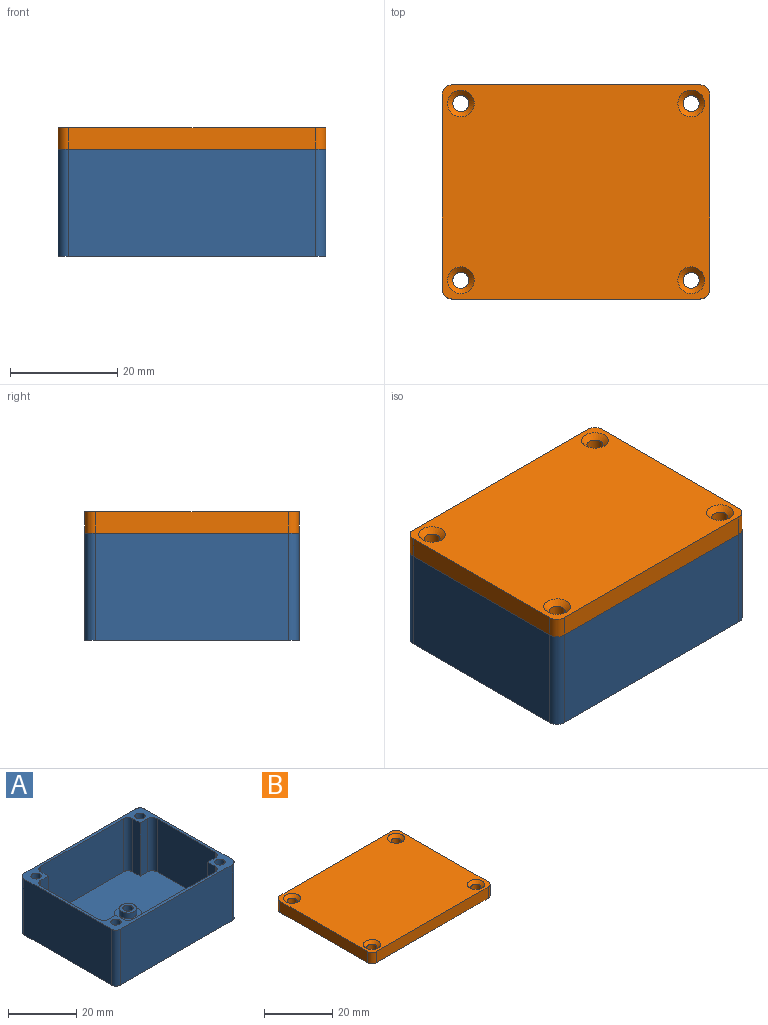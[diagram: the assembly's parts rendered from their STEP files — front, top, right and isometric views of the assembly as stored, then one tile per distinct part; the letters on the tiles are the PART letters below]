
ASSEMBLY  parts=2 mates=1
PART A: 47 faces, bbox 50x40x20 mm
  f0: plane 50x40mm, normal (0,0,-1), area 1936.5mm2, adj f8,f9,f10,f11,f20,f21,f22,f23
  f1: cylinder r=1.5mm len=4mm, axis (0,0,1), area 37.7mm2, adj f25,f34
  f2: plane 48x38mm, normal (0,0,1), area 1666.9mm2, adj f3,f4,f5,f6,f12,f13,f14,f15
  f3: plane 34x19mm, normal (0,-1,0), area 646mm2, adj f2,f7,f35,f41
  f4: plane 24x19mm, normal (1,0,0), area 456mm2, adj f2,f7,f39,f42
  f5: plane 24x19mm, normal (-1,0,0), area 456mm2, adj f2,f7,f36,f38
  f6: plane 34x19mm, normal (0,1,0), area 646mm2, adj f2,f7,f37,f40
  f7: plane 50x40mm, normal (0,0,1), area 251.2mm2, adj f3,f4,f5,f6,f8,f9,f10,f11
  f8: plane 46x20mm, normal (0,1,0), area 920mm2, adj f0,f7,f43,f46
  f9: plane 36x20mm, normal (-1,0,0), area 720mm2, adj f0,f7,f43,f44
  f10: plane 46x20mm, normal (0,-1,0), area 920mm2, adj f0,f7,f44,f45
  f11: plane 36x20mm, normal (1,0,0), area 720mm2, adj f0,f7,f45,f46
  f12: plane 19x3mm, normal (0,1,0), area 57mm2, adj f2,f7,f13,f39
  f13: plane 19x3mm, normal (1,0,0), area 57mm2, adj f2,f7,f12,f40
  f14: plane 19x3mm, normal (0,1,0), area 57mm2, adj f2,f7,f15,f38
  f15: plane 19x3mm, normal (-1,0,0), area 57mm2, adj f2,f7,f14,f37
  f16: plane 19x3mm, normal (0,-1,0), area 57mm2, adj f2,f7,f17,f36
  f17: plane 19x3mm, normal (-1,0,0), area 57mm2, adj f2,f7,f16,f35
  f18: plane 19x3mm, normal (0,-1,0), area 57mm2, adj f2,f7,f19,f42
  f19: plane 19x3mm, normal (1,0,0), area 57mm2, adj f2,f7,f18,f41
  f20: cylinder r=1.5mm len=20mm, axis (0,0,1), area 188.5mm2, adj f0,f7
  f21: cylinder r=1.5mm len=20mm, axis (0,0,1), area 188.5mm2, adj f0,f7
  f22: cylinder r=1.5mm len=20mm, axis (0,0,1), area 188.5mm2, adj f0,f7
  f23: cylinder r=1.5mm len=20mm, axis (0,0,1), area 188.5mm2, adj f0,f7
  f24: cylinder r=2.5mm len=5mm, axis (0,0,-1), area 31.4mm2, adj f25,f27
  f25: plane 5x5mm, normal (0,0,1), area 12.6mm2, adj f1,f24
  f26: cylinder r=4mm len=8mm, axis (0,0,-1), area 75.4mm2, adj f2,f27
  f27: plane 8x8mm, normal (0,0,1), area 30.6mm2, adj f24,f26
  f28: plane 2.56x2.39mm, normal (0.73,-0.68,0), area 7mm2, adj f0,f29,f33,f34
  f29: plane 3.41x2mm, normal (-0.23,-0.97,0), area 7mm2, adj f0,f28,f30,f34
  f30: plane 3.35x2mm, normal (-0.96,-0.29,0), area 7mm2, adj f0,f29,f31,f34
  f31: plane 2.56x2.39mm, normal (-0.73,0.68,0), area 7mm2, adj f0,f30,f32,f34
  f32: plane 3.41x2mm, normal (0.23,0.97,0), area 7mm2, adj f0,f31,f33,f34
  f33: plane 3.35x2mm, normal (0.96,0.29,0), area 7mm2, adj f0,f28,f32,f34
  f34: plane 6.82x6.7mm, normal (0,0,-1), area 24.8mm2, adj f1,f28,f29,f30,f31,f32,f33
  f35: cylinder r=2mm len=19mm, axis (0,0,-1), area 59.7mm2, adj f2,f3,f7,f17
  f36: cylinder r=2mm len=19mm, axis (0,0,1), area 59.7mm2, adj f2,f5,f7,f16
  f37: cylinder r=2mm len=19mm, axis (0,0,-1), area 59.7mm2, adj f2,f6,f7,f15
  f38: cylinder r=2mm len=19mm, axis (0,0,-1), area 59.7mm2, adj f2,f5,f7,f14
  f39: cylinder r=2mm len=19mm, axis (0,0,-1), area 59.7mm2, adj f2,f4,f7,f12
  f40: cylinder r=2mm len=19mm, axis (0,0,1), area 59.7mm2, adj f2,f6,f7,f13
  f41: cylinder r=2mm len=19mm, axis (0,0,1), area 59.7mm2, adj f2,f3,f7,f19
  f42: cylinder r=2mm len=19mm, axis (0,0,1), area 59.7mm2, adj f2,f4,f7,f18
  f43: cylinder r=2mm len=20mm, axis (0,0,1), area 62.8mm2, adj f0,f7,f8,f9
  f44: cylinder r=2mm len=20mm, axis (0,0,-1), area 62.8mm2, adj f0,f7,f9,f10
  f45: cylinder r=2mm len=20mm, axis (0,0,1), area 62.8mm2, adj f0,f7,f10,f11
  f46: cylinder r=2mm len=20mm, axis (0,0,-1), area 62.8mm2, adj f0,f7,f8,f11
PART B: 18 faces, bbox 50x40x4 mm
  f0: plane 46x4mm, normal (0,1,0), area 184mm2, adj f4,f5,f14,f17
  f1: plane 36x4mm, normal (-1,0,0), area 144mm2, adj f4,f5,f14,f15
  f2: plane 46x4mm, normal (0,-1,0), area 184mm2, adj f4,f5,f15,f16
  f3: plane 36x4mm, normal (1,0,0), area 144mm2, adj f4,f5,f16,f17
  f4: plane 50x40mm, normal (0,0,1), area 1918mm2, adj f0,f1,f2,f3,f10,f11,f12,f13
  f5: plane 50x40mm, normal (0,0,-1), area 1968.3mm2, adj f0,f1,f2,f3,f6,f7,f8,f9
  f6: cylinder r=1.5mm len=3mm, axis (0,0,1), area 28.3mm2, adj f5,f13
  f7: cylinder r=1.5mm len=3mm, axis (0,0,1), area 28.3mm2, adj f5,f11
  f8: cylinder r=1.5mm len=3mm, axis (0,0,1), area 28.3mm2, adj f5,f10
  f9: cylinder r=1.5mm len=3mm, axis (0,0,1), area 28.3mm2, adj f5,f12
  f10: cone r=1.5mm half-angle=45deg, axis (0,0,1), area 17.8mm2, adj f4,f8
  f11: cone r=1.5mm half-angle=45deg, axis (0,0,1), area 17.8mm2, adj f4,f7
  f12: cone r=1.5mm half-angle=45deg, axis (0,0,1), area 17.8mm2, adj f4,f9
  f13: cone r=1.5mm half-angle=45deg, axis (0,0,1), area 17.8mm2, adj f4,f6
  f14: cylinder r=2mm len=4mm, axis (0,0,1), area 12.6mm2, adj f0,f1,f4,f5
  f15: cylinder r=2mm len=4mm, axis (0,0,-1), area 12.6mm2, adj f1,f2,f4,f5
  f16: cylinder r=2mm len=4mm, axis (0,0,1), area 12.6mm2, adj f2,f3,f4,f5
  f17: cylinder r=2mm len=4mm, axis (0,0,-1), area 12.6mm2, adj f0,f3,f4,f5
PLACE A t=(2.79,-34.92,21.37)mm fixed
PLACE B t=(-70.21,-38.66,41.37)mm
MATE slider A.f21 <-> B.f7  axis (0,0,1) through (-12.26,-15.08,41.37)mm
